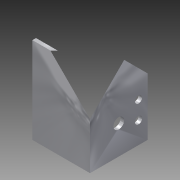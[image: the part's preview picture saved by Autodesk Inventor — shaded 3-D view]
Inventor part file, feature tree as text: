
AUTODESK INVENTOR PART (.ipt)
format: ipt  version: 2015 SP1 (Build 190203100, 203)  size: 130,048 bytes
history: native  units: in
note: dims shown in document units (in); Inventor stores cm internally (conversion verified against a paired STEP export)
features: sketch x4, extrude x2, hole x2
ambient origin geometry x8: Origin, YZ Plane, XZ Plane, XY Plane, X Axis, Y Axis, Z Axis, Center Point
bodies: Solid1 (feature_tree)
feature tree (8):
  extrude  "Extrusion1"  Depth=0.125in
  hole  "Hole1"  [1 undecoded]
  hole  "Hole2"  [1 undecoded]
  extrude  "Extrusion4"  Depth=3.0in
  sketch  "Sketch1"  dims[d0=2.0in d1=0.125in]
  sketch  "Sketch4"  dims[d2=0.125in d3=2.0in]
  sketch  "Sketch5"  dims[d4=3.0in d5=0.0in d11=1.0in]
  sketch  "Sketch6"  dims[d12=1.0in d13=0.375in d14=0.75in d15=0.375in d16=0.25in d17=0.5635in d18=1.0in d19=0.8108in d20=0.375in d21=0.25in d23=0.3125in d24=0.3125in d25=0.25in d26=0.75in d27=0.375in d28=0.25in d29=0.5635in d30=1.0in d31=0.8108in d32=1.0in d33=45.0deg d34=3.0in d35=0.0in]
note: 2 required parameter values undecoded (feature->parameter linkage not recoverable at this tier; creation-order binding heuristic only, values carry confidence <= 0.55)
